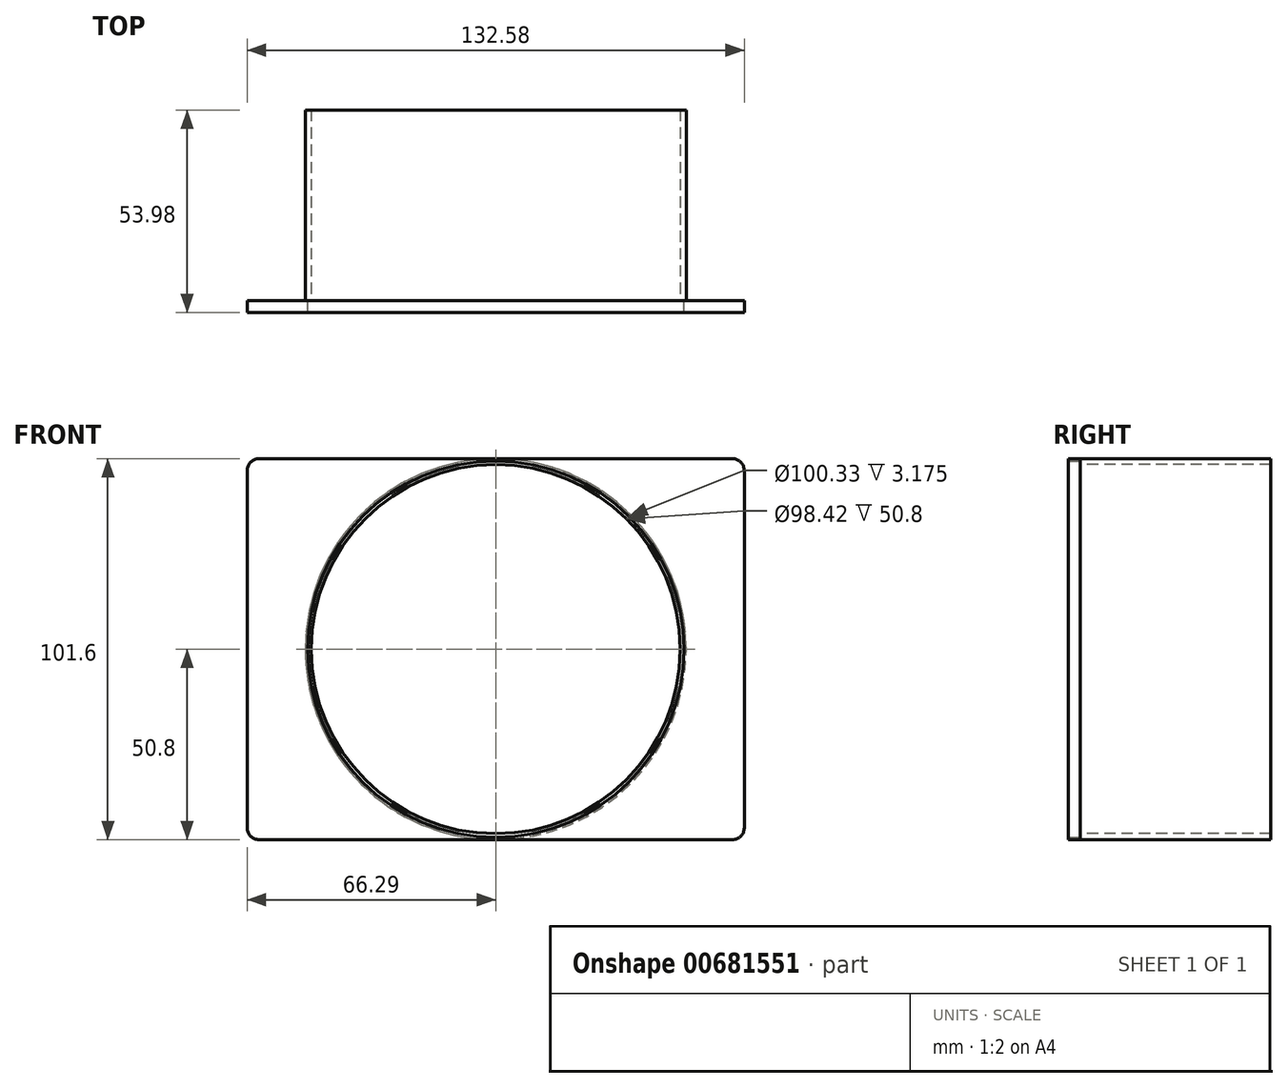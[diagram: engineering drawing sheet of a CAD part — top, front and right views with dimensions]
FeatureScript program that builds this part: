
annotation { "Feature Type Name" : "Feature", "Feature Type Description" : "" }
export const myFeature = defineFeature(function(context is Context, id is Id, definition is map)
    precondition{}
    {
        {
            var Q0;
            Q0=qCreatedBy(makeId("Front.planeOp"),FACE);
            var sketch = newSketch(context, id + "F0", { "sketchPlane" : qUnion([Q0])});
            skLineSegment(sketch, "E0.bottom", {"start": v(-63.12, 50.8) * mm, "end": v(63.12, 50.8) * mm});
            skLineSegment(sketch, "E0.top", {"start": v(-63.12, -50.8) * mm, "end": v(63.12, -50.8) * mm});
            skLineSegment(sketch, "E0.left", {"start": v(-66.3, 47.62) * mm, "end": v(-66.3, -47.62) * mm});
            skLineSegment(sketch, "E0.right", {"start": v(66.3, 47.62) * mm, "end": v(66.3, -47.62) * mm});
            skPoint(sketch, "E0.middle", {"position": v(0, 0) * mm});
            skPoint(sketch, "E1.visualSharp", {"position": v(66.3, 50.8) * mm});
            skArc(sketch, "E1.filletArc", {"start": v(66.3, 47.62) * mm, "mid": v(65.36, 49.87) * mm, "end": v(63.12, 50.8) * mm});
            skPoint(sketch, "E2.visualSharp", {"position": v(66.3, -50.8) * mm});
            skArc(sketch, "E2.filletArc", {"start": v(63.12, -50.8) * mm, "mid": v(65.36, -49.87) * mm, "end": v(66.3, -47.62) * mm});
            skPoint(sketch, "E3.visualSharp", {"position": v(-66.3, 50.8) * mm});
            skArc(sketch, "E3.filletArc", {"start": v(-63.12, 50.8) * mm, "mid": v(-65.36, 49.87) * mm, "end": v(-66.3, 47.62) * mm});
            skPoint(sketch, "E4.visualSharp", {"position": v(-66.3, -50.8) * mm});
            skArc(sketch, "E4.filletArc", {"start": v(-66.3, -47.62) * mm, "mid": v(-65.36, -49.87) * mm, "end": v(-63.12, -50.8) * mm});
            skCircle(sketch, "E5", {"center": v(0, 0) * mm, "radius": 50.17 * mm});
            skSolve(sketch);
        }
        {
            var Q0;
            Q0 = qSketchRegion(id + "F0", true);
            extrude(context, id + "F1", {"entities" : qUnion([Q0]), "depth" : 3.17 * mm, "offsetDistance" : 25.4 * mm});
        }
        {
            var Q0;
            Q0=makeQuery(id+"F1.opExtrude","CAP_FACE",FACE,{"disambiguationData":[OSD([sQuery(id+"F0.wireOp",EDGE,"E0.bottom"),sQuery(id+"F0.wireOp",EDGE,"E0.top"),sQuery(id+"F0.wireOp",EDGE,"E0.left"),sQuery(id+"F0.wireOp",EDGE,"E0.right"),sQuery(id+"F0.wireOp",EDGE,"E1.filletArc"),sQuery(id+"F0.wireOp",EDGE,"E2.filletArc"),sQuery(id+"F0.wireOp",EDGE,"E3.filletArc"),sQuery(id+"F0.wireOp",EDGE,"E4.filletArc"),sQuery(id+"F0.wireOp",EDGE,"E5")])],"isStart":true});
            var sketch = newSketch(context, id + "F2", { "sketchPlane" : qUnion([Q0])});
            skCircle(sketch, "E6", {"center": v(0, 0) * mm, "radius": 50.8 * mm});
            skCircle(sketch, "E7.0", {"center": v(0, 0) * mm, "radius": 49.21 * mm});
            skSolve(sketch);
        }
        {
            var Q0;
            Q0 = qSketchRegion(id + "F2", true);
            extrude(context, id + "F3", {"entities" : qUnion([Q0]), "operationType" : NewBodyOperationType.ADD, "depth" : 50.8 * mm, "offsetDistance" : 25.4 * mm});
        }
    });
